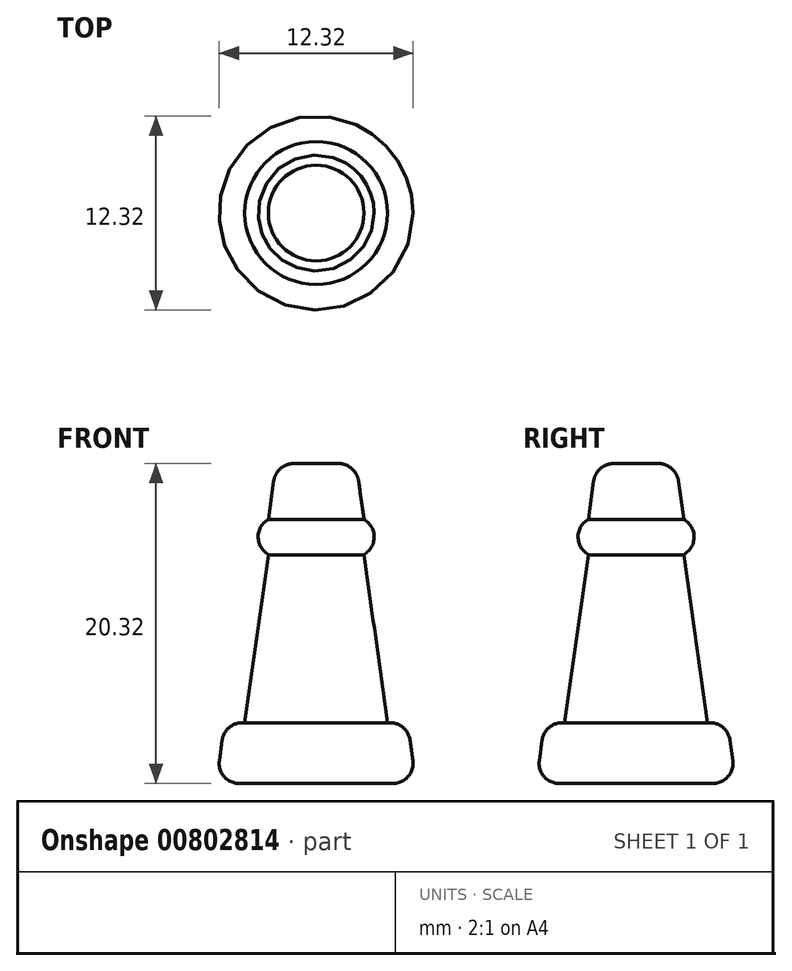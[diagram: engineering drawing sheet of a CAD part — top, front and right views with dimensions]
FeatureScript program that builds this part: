
annotation { "Feature Type Name" : "Feature", "Feature Type Description" : "" }
export const myFeature = defineFeature(function(context is Context, id is Id, definition is map)
    precondition{}
    {
        {
            var Q0;
            Q0=qCreatedBy(makeId("Front.planeOp"),FACE);
            var sketch = newSketch(context, id + "F0", { "sketchPlane" : qUnion([Q0])});
            skLineSegment(sketch, "E0", {"start": v(-6.35, 0) * mm, "end": v(-5.8, 3.86) * mm});
            skLineSegment(sketch, "E1", {"start": v(-5.8, 3.86) * mm, "end": v(-4.54, 3.86) * mm});
            skLineSegment(sketch, "E2", {"start": v(-4.54, 3.86) * mm, "end": v(-3.04, 14.52) * mm});
            skLineSegment(sketch, "E3", {"start": v(-3.04, 14.52) * mm, "end": v(-4.54, 15.81) * mm});
            skLineSegment(sketch, "E4", {"start": v(-4.54, 15.81) * mm, "end": v(-3.04, 16.76) * mm});
            skLineSegment(sketch, "E5", {"start": v(-3.04, 16.76) * mm, "end": v(-2.65, 19.51) * mm});
            skLineSegment(sketch, "E6", {"start": v(-2.65, 19.51) * mm, "end": v(-2.07, 20.32) * mm});
            skLineSegment(sketch, "E7", {"start": v(-2.07, 20.32) * mm, "end": v(0, 20.32) * mm});
            skLineSegment(sketch, "E8", {"start": v(0, 20.32) * mm, "end": v(0, 0) * mm});
            skLineSegment(sketch, "E9", {"start": v(0, 0) * mm, "end": v(-6.35, 0) * mm});
            skSolve(sketch);
        }
        {
            var Q0;
            Q0=makeQuery(id+"F0.imprint","IMPRINT",FACE,{"disambiguationData":[TD([[makeQuery(id+"F0.imprint","IMPRINT",EDGE,{"derivedFrom":sQuery(id+"F0.wireOp",EDGE,"E0")}),-1.0]])]});
            var Q1;
            Q1=sQuery(id+"F0.wireOp",EDGE,"E8");
            revolve(context, id + "F1", {"surfaceOperationType" : NewSurfaceOperationType.NEW, "entities" : qUnion([Q0]), "axis" : qUnion([Q1]), "revolveType" : RevolveType.FULL});
        }
        {
            var Q0;
            Q0=makeQuery(id+"F1.opRevolve","SWEPT_FACE",FACE,{"disambiguationData":[OSD([sQuery(id+"F0.wireOp",EDGE,"E6")])]});
            fillet(context, id + "F2", {"entities" : qUnion([Q0]), "radius" : 1.27 * mm, "tangentPropagation" : true, "allowEdgeOverflow" : false});
        }
        {
            var Q0;
            Q0=makeQuery(id+"F1.opRevolve","SWEPT_EDGE",EDGE,{"disambiguationData":[OSD([sQuery(id+"F0.wireOp",EDGE,"E0"),sQuery(id+"F0.wireOp",EDGE,"E1")])]});
            var Q1;
            Q1=makeQuery(id+"F1.opRevolve","SWEPT_EDGE",EDGE,{"disambiguationData":[OSD([sQuery(id+"F0.wireOp",EDGE,"E6"),sQuery(id+"F0.wireOp",EDGE,"E7")])]});
            var Q2;
            Q2=makeQuery(id+"F1.opRevolve","SWEPT_EDGE",EDGE,{"disambiguationData":[OSD([sQuery(id+"F0.wireOp",EDGE,"E3"),sQuery(id+"F0.wireOp",EDGE,"E4")])]});
            var Q3;
            Q3=makeQuery(id+"F1.opRevolve","SWEPT_EDGE",EDGE,{"disambiguationData":[OSD([sQuery(id+"F0.wireOp",EDGE,"E0"),sQuery(id+"F0.wireOp",EDGE,"E9")])]});
            fillet(context, id + "F3", {"entities" : qUnion([Q0, Q1, Q2, Q3]), "radius" : 1.27 * mm, "tangentPropagation" : true, "allowEdgeOverflow" : false});
        }
    });
